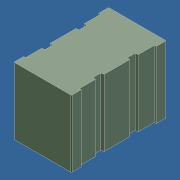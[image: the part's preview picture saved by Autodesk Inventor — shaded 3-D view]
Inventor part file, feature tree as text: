
AUTODESK INVENTOR PART (.ipt)
format: ipt  version: 2014 (Build 180170000, 170)  size: 143,872 bytes
history: native  units: in
note: dims shown in document units (in); Inventor stores cm internally (conversion verified against a paired STEP export)
features: other x21, extrude x3, sketch x3, pattern_linear x1
ambient origin geometry x8: Origin, YZ Plane, XZ Plane, XY Plane, X Axis, Y Axis, Z Axis, Center Point
bodies: Solid1 (feature_tree)
feature tree (28):
  extrude  "Extrusion1"  Depth=0.001in TaperAngle=0.0deg
  extrude  "Extrusion2"  Depth=0.185in TaperAngle=0.0deg
  extrude  "Extrusion3"  [1 undecoded]
  pattern_linear  "Rectangular Pattern1"  [2 undecoded]
  other  "rot_XY"
  other  "rot_YZ"
  other  "rot_ZX"
  other  "rot_X"
  other  "rot_Y"
  other  "rot_Z"
  other  "rot_Center"
  other  "to_cover_XY"
  other  "to_cover_YZ"
  other  "to_cover_ZX"
  other  "to_cover_X"
  other  "to_cover_Y"
  other  "to_cover_Z"
  other  "to_cover_Center"
  other  "to_terminals_XY"
  other  "to_terminals_YZ"
  other  "to_terminals_ZX"
  other  "to_terminals_X"
  other  "to_terminals_Y"
  other  "to_terminals_Z"
  other  "to_terminals_Center"
  sketch  "Sketch_2"  dims[d4=0.01in d5=0.0in d6=1.1811in d8=0.185in d9=0.3937in d11=0.0in]
  sketch  "Sketch_1"  dims[d0=0.361in d1=0.0in d2=0.001in d3=0.0in]
  sketch  "Sketch_7"
note: 3 required parameter values undecoded (feature->parameter linkage not recoverable at this tier; creation-order binding heuristic only, values carry confidence <= 0.55)
